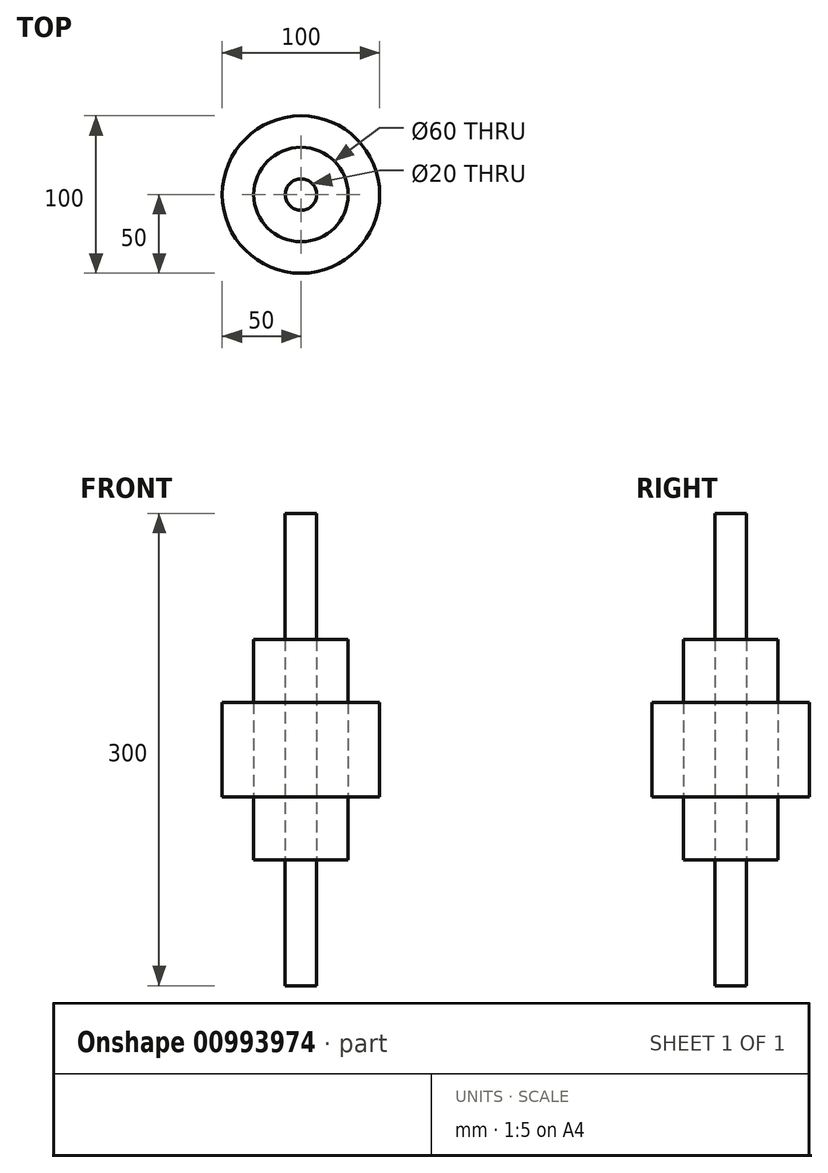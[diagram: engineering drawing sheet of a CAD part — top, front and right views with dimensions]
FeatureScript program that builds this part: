
annotation { "Feature Type Name" : "Feature", "Feature Type Description" : "" }
export const myFeature = defineFeature(function(context is Context, id is Id, definition is map)
    precondition{}
    {
        {
            var Q0;
            Q0=qCreatedBy(makeId("Top.planeOp"),FACE);
            var sketch = newSketch(context, id + "F0", { "sketchPlane" : qUnion([Q0])});
            skCircle(sketch, "E0", {"center": v(0, 0) * mm, "radius": 50 * mm});
            skCircle(sketch, "E1", {"center": v(0, 0) * mm, "radius": 30 * mm});
            skCircle(sketch, "E2", {"center": v(0, 0) * mm, "radius": 10 * mm});
            skSolve(sketch);
        }
        {
            var Q0;
            Q0=makeQuery(id+"F0.imprint","IMPRINT",FACE,{"disambiguationData":[TD([[makeQuery(id+"F0.imprint","IMPRINT",EDGE,{"derivedFrom":sQuery(id+"F0.wireOp",EDGE,"E2")}),1.0]])]});
            extrude(context, id + "F1", {"entities" : qUnion([Q0]), "endBound" : BoundingType.SYMMETRIC, "depth" : 300 * mm, "offsetDistance" : 25 * mm});
        }
        {
            var Q0;
            Q0=makeQuery(id+"F0.imprint","IMPRINT",FACE,{"disambiguationData":[TD([[makeQuery(id+"F0.imprint","IMPRINT",EDGE,{"derivedFrom":sQuery(id+"F0.wireOp",EDGE,"E0")}),1.0]])]});
            extrude(context, id + "F2", {"entities" : qUnion([Q0]), "endBound" : BoundingType.SYMMETRIC, "depth" : 60 * mm, "offsetDistance" : 25 * mm});
        }
        {
            var Q0;
            Q0=makeQuery(id+"F0.imprint","IMPRINT",FACE,{"disambiguationData":[TD([[makeQuery(id+"F0.imprint","IMPRINT",EDGE,{"derivedFrom":sQuery(id+"F0.wireOp",EDGE,"E1")}),1.0]])]});
            extrude(context, id + "F3", {"entities" : qUnion([Q0]), "endBound" : BoundingType.SYMMETRIC, "depth" : 140 * mm, "offsetDistance" : 25 * mm});
        }
    });
